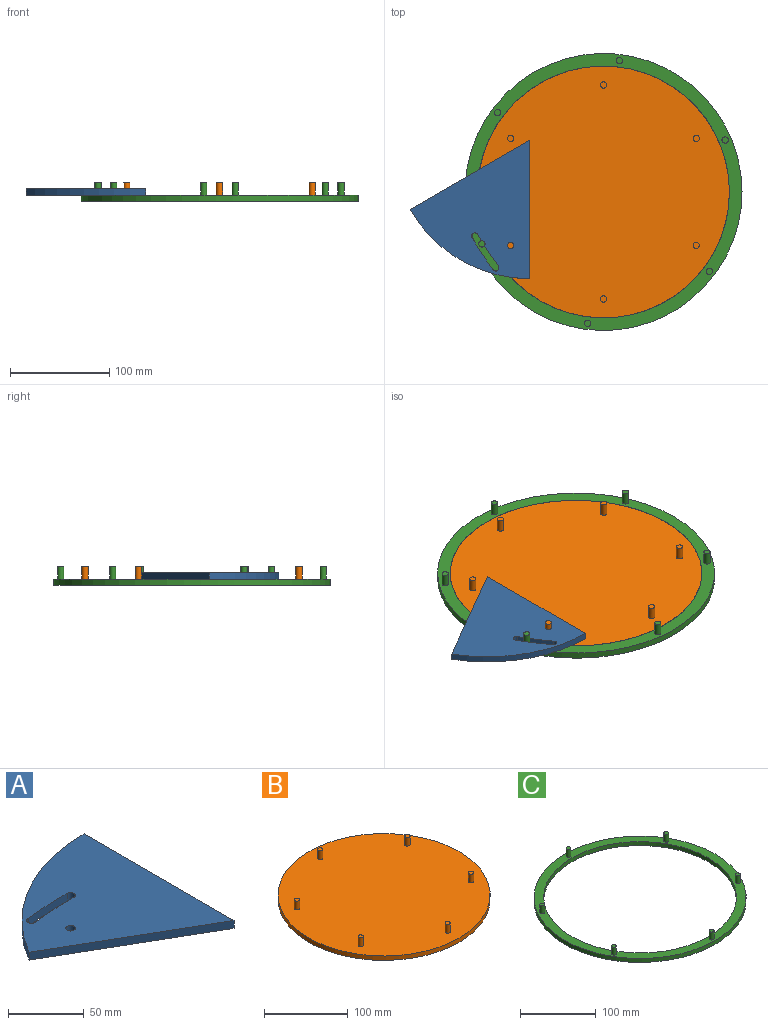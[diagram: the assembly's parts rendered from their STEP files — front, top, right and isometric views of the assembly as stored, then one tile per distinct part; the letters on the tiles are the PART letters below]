
ASSEMBLY  parts=3 mates=3
PART A: 10 faces, bbox 121x139.7x6.4 mm
  f0: cylinder r=3.17mm len=6.35mm, axis (0,0,-1), area 63.3mm2, adj f1,f5,f8,f9
  f1: cylinder r=254mm len=37.94mm, axis (0,0,-1), area 241.5mm2, adj f0,f2,f8,f9
  f2: cylinder r=3.17mm len=6.35mm, axis (0,0,-1), area 68.2mm2, adj f1,f5,f8,f9
  f3: plane 120.98x69.85mm, normal (-0.5,-0.87,0), area 887.1mm2, adj f4,f6,f8,f9
  f4: plane 139.7x6.35mm, normal (1,0,0), area 887.1mm2, adj f3,f6,f8,f9
  f5: cylinder r=254mm len=38.13mm, axis (0,0,-1), area 242.7mm2, adj f0,f2,f8,f9
  f6: cylinder r=139.7mm len=120.98mm, axis (0,0,-1), area 929mm2, adj f3,f4,f8,f9
  f7: cylinder r=3.17mm len=6.35mm, axis (0,0,-1), area 126.7mm2, adj f8,f9
  f8: plane 139.7x120.98mm, normal (0,0,1), area 9912mm2, adj f0,f1,f2,f3,f4,f5,f6,f7
  f9: plane 139.7x120.98mm, normal (0,0,-1), area 9912mm2, adj f0,f1,f2,f3,f4,f5,f6,f7
PART B: 15 faces, bbox 254x254x19.1 mm
  f0: cylinder r=3.17mm len=12.7mm, axis (0,0,-1), area 253.4mm2, adj f1,f12
  f1: plane 6.35x6.35mm, normal (0,0,1), area 31.7mm2, adj f0
  f2: cylinder r=3.17mm len=12.7mm, axis (0,0,-1), area 253.4mm2, adj f3,f12
  f3: plane 6.35x6.35mm, normal (0,0,1), area 31.7mm2, adj f2
  f4: cylinder r=3.17mm len=12.7mm, axis (0,0,-1), area 253.4mm2, adj f5,f12
  f5: plane 6.35x6.35mm, normal (0,0,1), area 31.7mm2, adj f4
  f6: cylinder r=3.17mm len=12.7mm, axis (0,0,-1), area 253.4mm2, adj f7,f12
  f7: plane 6.35x6.35mm, normal (0,0,1), area 31.7mm2, adj f6
  f8: cylinder r=3.17mm len=12.7mm, axis (0,0,-1), area 253.4mm2, adj f9,f12
  f9: plane 6.35x6.35mm, normal (0,0,1), area 31.7mm2, adj f8
  f10: cylinder r=127mm len=254mm, axis (0,0,1), area 5067.1mm2, adj f11,f12
  f11: plane 254x254mm, normal (0,0,-1), area 50670.7mm2, adj f10
  f12: plane 254x254mm, normal (0,0,1), area 50480.7mm2, adj f0,f2,f4,f6,f8,f10,f13
  f13: cylinder r=3.17mm len=12.7mm, axis (0,0,-1), area 253.4mm2, adj f12,f14
  f14: plane 6.35x6.35mm, normal (0,0,1), area 31.7mm2, adj f13
PART C: 16 faces, bbox 279.4x279.4x19.1 mm
  f0: cylinder r=3.17mm len=12.7mm, axis (0,0,-1), area 253.4mm2, adj f1,f15
  f1: plane 6.35x6.35mm, normal (0,0,1), area 31.7mm2, adj f0
  f2: cylinder r=3.17mm len=12.7mm, axis (0,0,-1), area 253.4mm2, adj f3,f15
  f3: plane 6.35x6.35mm, normal (0,0,1), area 31.7mm2, adj f2
  f4: cylinder r=3.17mm len=12.7mm, axis (0,0,-1), area 253.4mm2, adj f5,f15
  f5: plane 6.35x6.35mm, normal (0,0,1), area 31.7mm2, adj f4
  f6: cylinder r=3.17mm len=12.7mm, axis (0,0,-1), area 253.4mm2, adj f7,f15
  f7: plane 6.35x6.35mm, normal (0,0,1), area 31.7mm2, adj f6
  f8: cylinder r=3.17mm len=12.7mm, axis (0,0,-1), area 253.4mm2, adj f9,f15
  f9: plane 6.35x6.35mm, normal (0,0,1), area 31.7mm2, adj f8
  f10: cylinder r=3.17mm len=12.7mm, axis (0,0,-1), area 253.4mm2, adj f11,f15
  f11: plane 6.35x6.35mm, normal (0,0,1), area 31.7mm2, adj f10
  f12: cylinder r=127mm len=254mm, axis (0,0,1), area 5067.1mm2, adj f14,f15
  f13: cylinder r=139.7mm len=279.4mm, axis (0,0,1), area 5573.8mm2, adj f14,f15
  f14: plane 279.4x279.4mm, normal (0,0,-1), area 10640.9mm2, adj f12,f13
  f15: plane 279.4x279.4mm, normal (0,0,1), area 10450.8mm2, adj f0,f2,f4,f6,f8,f10,f12,f13
PLACE A rot(axis=(0,0,1),120deg) t=(-74.14,52.23,6.35)mm
PLACE B t=(0,0,6.35)mm
PLACE C rot(axis=(0,0,-1),6.9deg) t=(0,0,6.35)mm
MATE revolute C.f13 <-> B.f10  axis (0,0,-1) through (0,0,0)mm
MATE pin_slot C.f8 <-> A.f2  axis (0,0,-1) through (-122.63,-52.38,12.7)mm
MATE revolute A.f7 <-> B.f4  axis (0,0,-1) through (-93.49,-53.98,6.35)mm
